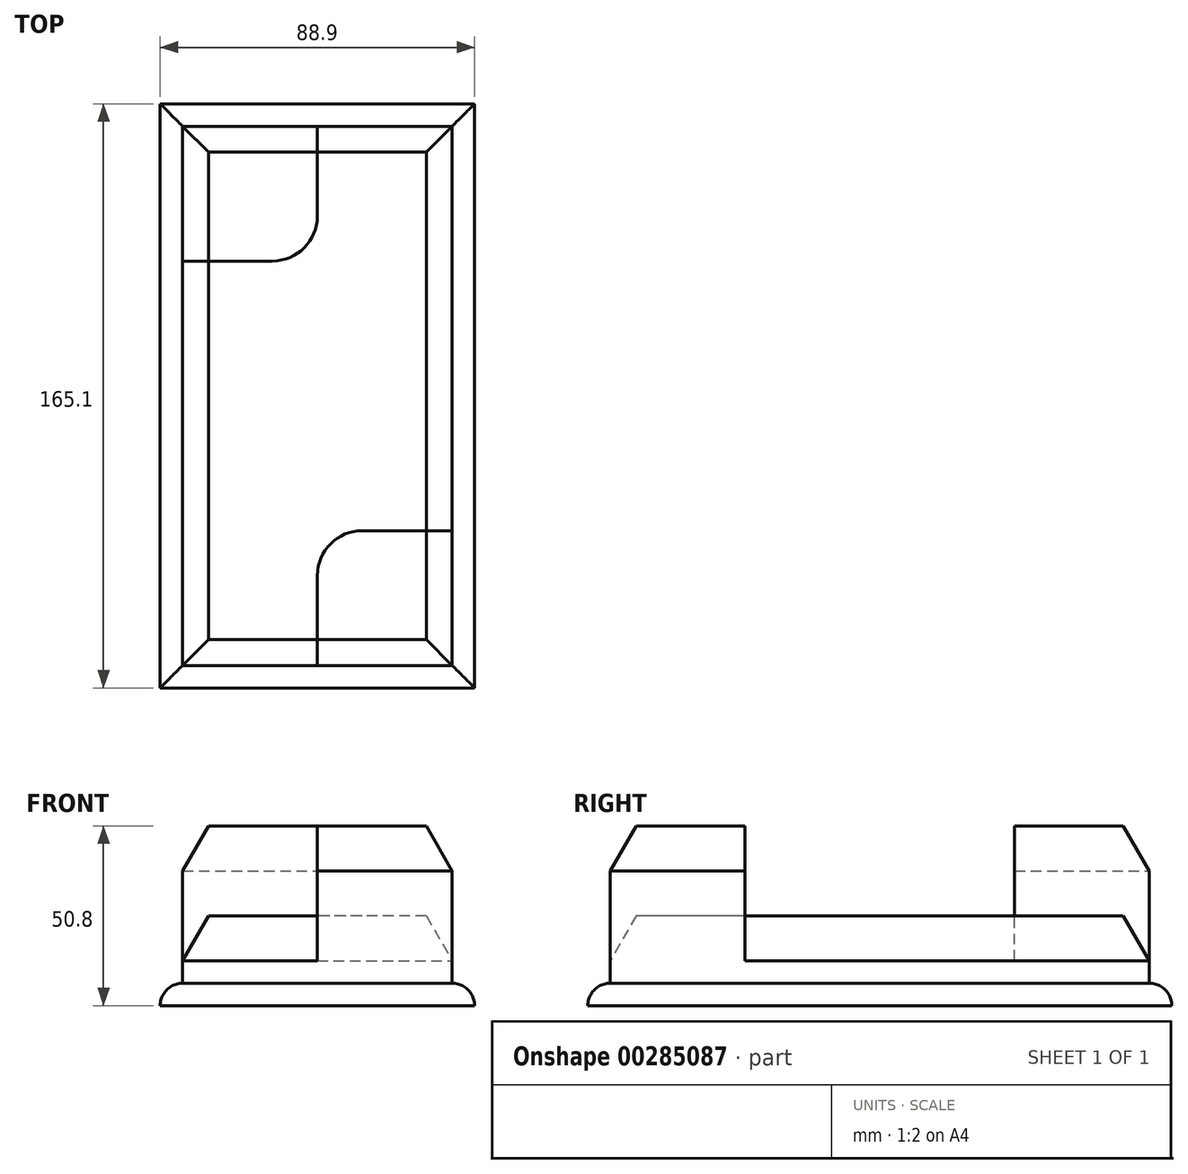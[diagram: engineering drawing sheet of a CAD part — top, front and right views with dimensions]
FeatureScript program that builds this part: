
annotation { "Feature Type Name" : "Feature", "Feature Type Description" : "" }
export const myFeature = defineFeature(function(context is Context, id is Id, definition is map)
    precondition{}
    {
        {
            var Q0;
            Q0=qCreatedBy(makeId("Top.planeOp"),FACE);
            var sketch = newSketch(context, id + "F0", { "sketchPlane" : qUnion([Q0])});
            skLineSegment(sketch, "E0.bottom", {"start": v(-42.6, 79.88) * mm, "end": v(33.6, 79.88) * mm});
            skLineSegment(sketch, "E0.top", {"start": v(-42.6, -72.52) * mm, "end": v(33.6, -72.52) * mm});
            skLineSegment(sketch, "E0.left", {"start": v(-42.6, 79.88) * mm, "end": v(-42.6, -72.52) * mm});
            skLineSegment(sketch, "E0.right", {"start": v(33.6, 79.88) * mm, "end": v(33.6, -72.52) * mm});
            skLineSegment(sketch, "E1", {"start": v(-4.5, 79.88) * mm, "end": v(-4.5, 54.48) * mm});
            skLineSegment(sketch, "E2", {"start": v(-17.2, 41.78) * mm, "end": v(-42.6, 41.78) * mm});
            skLineSegment(sketch, "E3", {"start": v(-4.5, -72.52) * mm, "end": v(-4.5, -47.12) * mm});
            skLineSegment(sketch, "E4", {"start": v(8.2, -34.42) * mm, "end": v(33.6, -34.42) * mm});
            skPoint(sketch, "E5.visualSharp", {"position": v(-4.5, 41.78) * mm});
            skArc(sketch, "E5.filletArc", {"start": v(-17.2, 41.78) * mm, "mid": v(-8.23, 45.5) * mm, "end": v(-4.5, 54.48) * mm});
            skPoint(sketch, "E6.visualSharp", {"position": v(-4.5, -34.42) * mm});
            skArc(sketch, "E6.filletArc", {"start": v(8.2, -34.42) * mm, "mid": v(-0.79, -38.14) * mm, "end": v(-4.5, -47.12) * mm});
            skLineSegment(sketch, "E7.0", {"start": v(-48.96, 86.23) * mm, "end": v(39.94, 86.23) * mm});
            skLineSegment(sketch, "E7.1", {"start": v(-48.96, 86.23) * mm, "end": v(-48.96, -78.87) * mm});
            skLineSegment(sketch, "E7.2", {"start": v(-48.96, -78.87) * mm, "end": v(39.94, -78.87) * mm});
            skLineSegment(sketch, "E7.3", {"start": v(39.94, 86.23) * mm, "end": v(39.94, -78.87) * mm});
            skSolve(sketch);
        }
        {
            var Q0;
            {var subQ9=sQuery(id+"F0.wireOp",EDGE,"E1");Q0=makeQuery(id+"F0.imprint","IMPRINT",FACE,{"disambiguationData":[TD([[makeQuery(id+"F0.imprint","IMPRINT",EDGE,{"derivedFrom":subQ9}),1.0]])]});}
            var Q1;
            {var subQ1=sQuery(id+"F0.wireOp",EDGE,"E3");Q1=makeQuery(id+"F0.imprint","IMPRINT",FACE,{"disambiguationData":[TD([[makeQuery(id+"F0.imprint","IMPRINT",EDGE,{"derivedFrom":subQ1}),-1.0]])]});}
            var Q2;
            {var subQ0=sQuery(id+"F0.wireOp",EDGE,"E1");Q2=makeQuery(id+"F0.imprint","IMPRINT",FACE,{"disambiguationData":[TD([[makeQuery(id+"F0.imprint","IMPRINT",EDGE,{"derivedFrom":subQ0}),-1.0]])]});}
            extrude(context, id + "F1", {"entities" : qUnion([Q0, Q1, Q2]), "depth" : 25.4 * mm});
        }
        {
            var Q0;
            {var subQ1=sQuery(id+"F0.wireOp",EDGE,"E3");Q0=makeQuery(id+"F0.imprint","IMPRINT",FACE,{"disambiguationData":[TD([[makeQuery(id+"F0.imprint","IMPRINT",EDGE,{"derivedFrom":subQ1}),-1.0]])]});}
            var Q1;
            {var subQ0=sQuery(id+"F0.wireOp",EDGE,"E1");Q1=makeQuery(id+"F0.imprint","IMPRINT",FACE,{"disambiguationData":[TD([[makeQuery(id+"F0.imprint","IMPRINT",EDGE,{"derivedFrom":subQ0}),-1.0]])]});}
            extrude(context, id + "F2", {"entities" : qUnion([Q0, Q1]), "operationType" : NewBodyOperationType.ADD, "depth" : 50.8 * mm});
        }
        {
            var Q0;
            Q0=makeQuery(id+"F0.imprint","IMPRINT",FACE,{"disambiguationData":[TD([[makeQuery(id+"F0.imprint","IMPRINT",EDGE,{"derivedFrom":sQuery(id+"F0.wireOp",EDGE,"E7.0")}),-1.0]])]});
            extrude(context, id + "F3", {"entities" : qUnion([Q0]), "operationType" : NewBodyOperationType.ADD, "depth" : 6.35 * mm});
        }
        {
            var Q0;
            Q0=makeQuery(id+"F3.opExtrude","CAP_EDGE",EDGE,{"disambiguationData":[OSD([sQuery(id+"F0.wireOp",EDGE,"E7.2")])],"isStart":false});
            var Q1;
            Q1=makeQuery(id+"F3.opExtrude","CAP_EDGE",EDGE,{"disambiguationData":[OSD([sQuery(id+"F0.wireOp",EDGE,"E7.3")])],"isStart":false});
            var Q2;
            Q2=makeQuery(id+"F3.opExtrude","CAP_EDGE",EDGE,{"disambiguationData":[OSD([sQuery(id+"F0.wireOp",EDGE,"E7.1")])],"isStart":false});
            var Q3;
            Q3=makeQuery(id+"F3.opExtrude","CAP_EDGE",EDGE,{"disambiguationData":[OSD([sQuery(id+"F0.wireOp",EDGE,"E7.0")])],"isStart":false});
            fillet(context, id + "F4", {"entities" : qUnion([Q0, Q1, Q2, Q3]), "radius" : 6.35 * mm, "tangentPropagation" : true, "allowEdgeOverflow" : false});
        }
        {
            var Q0;
            Q0=makeQuery(id+"F1.opExtrude","CAP_EDGE",EDGE,{"disambiguationData":[OSD([sQuery(id+"F0.wireOp",EDGE,"E0.right")])],"isStart":false});
            var Q1;
            Q1=makeQuery(id+"F1.opExtrude","CAP_EDGE",EDGE,{"disambiguationData":[OSD([sQuery(id+"F0.wireOp",EDGE,"E0.bottom")])],"isStart":false});
            var Q2;
            Q2=makeQuery(id+"F1.opExtrude","CAP_EDGE",EDGE,{"disambiguationData":[OSD([sQuery(id+"F0.wireOp",EDGE,"E0.top")])],"isStart":false});
            var Q3;
            Q3=makeQuery(id+"F1.opExtrude","CAP_EDGE",EDGE,{"disambiguationData":[OSD([sQuery(id+"F0.wireOp",EDGE,"E0.left")])],"isStart":false});
            chamfer(context, id + "F5", {"entities" : qUnion([Q0, Q1, Q2, Q3]), "chamferType" : ChamferType.OFFSET_ANGLE, "width" : 12.7 * mm, "oppositeDirection" : false, "angle" : 30 * degree, "tangentPropagation" : true});
        }
        {
            var Q0;
            Q0=makeQuery(id+"F2.opExtrude","CAP_EDGE",EDGE,{"disambiguationData":[OSD([sQuery(id+"F0.wireOp",EDGE,"E0.top")])],"isStart":false});
            var Q1;
            Q1=makeQuery(id+"F2.opExtrude","CAP_EDGE",EDGE,{"disambiguationData":[OSD([sQuery(id+"F0.wireOp",EDGE,"E0.right")])],"isStart":false});
            chamfer(context, id + "F6", {"entities" : qUnion([Q0, Q1]), "chamferType" : ChamferType.OFFSET_ANGLE, "width" : 12.7 * mm, "oppositeDirection" : true, "angle" : 30 * degree, "tangentPropagation" : true});
        }
        {
            var Q0;
            Q0=makeQuery(id+"F2.opExtrude","CAP_EDGE",EDGE,{"disambiguationData":[OSD([sQuery(id+"F0.wireOp",EDGE,"E0.bottom")])],"isStart":false});
            var Q1;
            Q1=makeQuery(id+"F2.opExtrude","CAP_EDGE",EDGE,{"disambiguationData":[OSD([sQuery(id+"F0.wireOp",EDGE,"E0.left")])],"isStart":false});
            chamfer(context, id + "F7", {"entities" : qUnion([Q0, Q1]), "chamferType" : ChamferType.OFFSET_ANGLE, "width" : 12.7 * mm, "oppositeDirection" : false, "angle" : 30 * degree, "tangentPropagation" : true});
        }
    });
